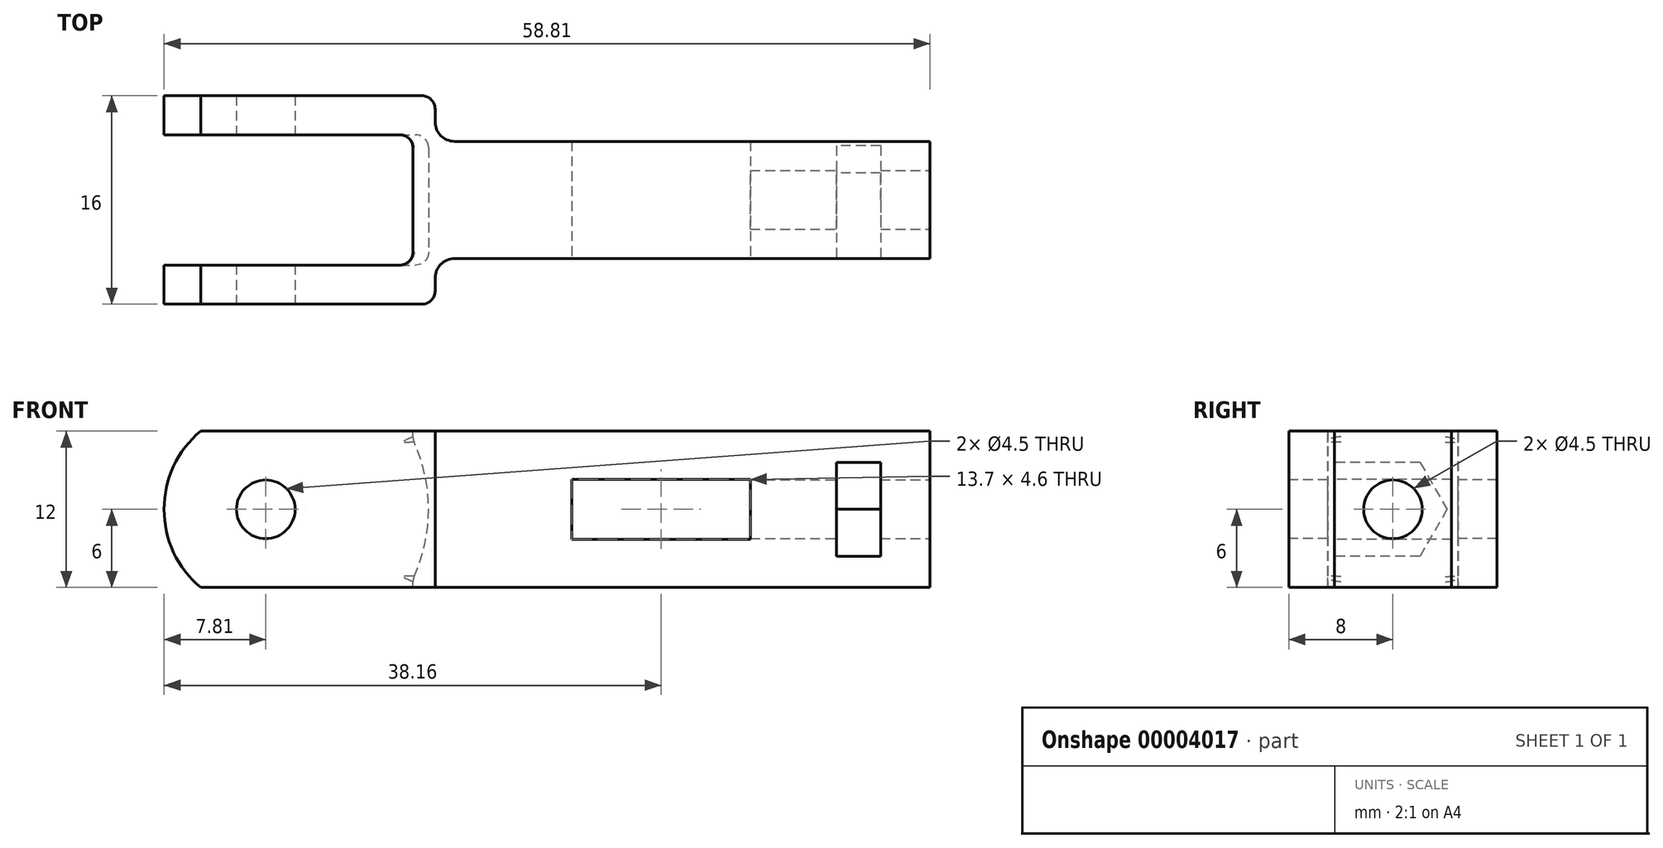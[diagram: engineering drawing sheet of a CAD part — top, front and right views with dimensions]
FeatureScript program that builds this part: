
annotation { "Feature Type Name" : "Feature", "Feature Type Description" : "" }
export const myFeature = defineFeature(function(context is Context, id is Id, definition is map)
    precondition{}
    {
        {
            var Q0;
            Q0=qCreatedBy(makeId("Top.planeOp"),FACE);
            var sketch = newSketch(context, id + "F0", { "sketchPlane" : qUnion([Q0])});
            skLineSegment(sketch, "E0", {"start": v(-5, 8) * mm, "end": v(-5, -8) * mm});
            skLineSegment(sketch, "E1", {"start": v(-5, 8) * mm, "end": v(13, 8) * mm});
            skLineSegment(sketch, "E2", {"start": v(13, 8) * mm, "end": v(13, 4.5) * mm});
            skLineSegment(sketch, "E3", {"start": v(13, 4.5) * mm, "end": v(51, 4.5) * mm});
            skLineSegment(sketch, "E4", {"start": v(51, 4.5) * mm, "end": v(51, -4.5) * mm});
            skLineSegment(sketch, "E5", {"start": v(51, -4.5) * mm, "end": v(13, -4.5) * mm});
            skLineSegment(sketch, "E6", {"start": v(13, -4.5) * mm, "end": v(13, -8) * mm});
            skLineSegment(sketch, "E7", {"start": v(13, -8) * mm, "end": v(-5, -8) * mm});
            skLineSegment(sketch, "E8", {"start": v(0, 0) * mm, "end": v(51, 0) * mm, "construction": true});
            skSolve(sketch);
        }
        {
            var Q0;
            Q0=makeQuery(id+"F0.imprint","IMPRINT",FACE,{"disambiguationData":[TD([[makeQuery(id+"F0.imprint","IMPRINT",EDGE,{"derivedFrom":sQuery(id+"F0.wireOp",EDGE,"E0")}),1.0]])]});
            extrude(context, id + "F1", {"entities" : qUnion([Q0]), "depth" : 12 * mm, "symmetric" : true});
        }
        {
            var Q0;
            Q0=makeQuery(id+"F1.opExtrude","SWEPT_FACE",FACE,{"disambiguationData":[OSD([sQuery(id+"F0.wireOp",EDGE,"E7")])]});
            var sketch = newSketch(context, id + "F2", { "sketchPlane" : qUnion([Q0])});
            skCircle(sketch, "E9", {"center": v(0, 0) * mm, "radius": 2.25 * mm});
            skSolve(sketch);
        }
        {
            var Q0;
            Q0=makeQuery(id+"F2.imprint","IMPRINT",FACE,{"disambiguationData":[TD([[makeQuery(id+"F2.imprint","IMPRINT",EDGE,{"derivedFrom":sQuery(id+"F2.wireOp",EDGE,"E9")}),1.0]])]});
            extrude(context, id + "F3", {"entities" : qUnion([Q0]), "operationType" : NewBodyOperationType.REMOVE, "endBound" : BoundingType.THROUGH_ALL, "oppositeDirection" : true, "depth" : 25 * mm});
        }
        {
            var Q0;
            Q0=makeQuery(id+"F1.opExtrude","SWEPT_FACE",FACE,{"disambiguationData":[OSD([sQuery(id+"F0.wireOp",EDGE,"E7")])]});
            var sketch = newSketch(context, id + "F4", { "sketchPlane" : qUnion([Q0])});
            skArc(sketch, "E10", {"start": v(-5, 6) * mm, "mid": v(-7.81, 0) * mm, "end": v(-5, -6) * mm});
            skLineSegment(sketch, "E11", {"start": v(-5, -6) * mm, "end": v(-5, 6) * mm});
            skSolve(sketch);
        }
        {
            var Q0;
            Q0=makeQuery(id+"F4.imprint","IMPRINT",FACE,{"disambiguationData":[TD([[makeQuery(id+"F4.imprint","IMPRINT",EDGE,{"derivedFrom":sQuery(id+"F4.wireOp",EDGE,"E10")}),1.0]])]});
            var Q1;
            Q1=makeQuery(id+"F1.opExtrude","SWEPT_FACE",FACE,{"disambiguationData":[OSD([sQuery(id+"F0.wireOp",EDGE,"E1")])]});
            extrude(context, id + "F5", {"entities" : qUnion([Q0]), "operationType" : NewBodyOperationType.ADD, "endBound" : BoundingType.UP_TO_SURFACE, "oppositeDirection" : true, "endBoundEntityFace" : qUnion([Q1]), "depth" : 25 * mm});
        }
        {
            var Q0;
            Q0=makeQuery(id+"F1.opExtrude","SWEPT_EDGE",EDGE,{"disambiguationData":[OSD([sQuery(id+"F0.wireOp",EDGE,"E2"),sQuery(id+"F0.wireOp",EDGE,"E3")])]});
            var Q1;
            Q1=makeQuery(id+"F1.opExtrude","SWEPT_EDGE",EDGE,{"disambiguationData":[OSD([sQuery(id+"F0.wireOp",EDGE,"E5"),sQuery(id+"F0.wireOp",EDGE,"E6")])]});
            fillet(context, id + "F6", {"entities" : qUnion([Q0, Q1]), "radius" : 1.5 * mm, "tangentPropagation" : true, "allowEdgeOverflow" : false});
        }
        {
            var Q0;
            Q0=qCreatedBy(makeId("Front.planeOp"),FACE);
            var sketch = newSketch(context, id + "F7", { "sketchPlane" : qUnion([Q0])});
            skArc(sketch, "E12", {"start": v(11.3, -5.34) * mm, "mid": v(12.5, 0) * mm, "end": v(11.3, 5.34) * mm});
            skLineSegment(sketch, "E13", {"start": v(11.3, 5.34) * mm, "end": v(11.3, 6) * mm});
            skLineSegment(sketch, "E14", {"start": v(-5, -6) * mm, "end": v(11.3, -6) * mm});
            skLineSegment(sketch, "E15", {"start": v(11.3, -6) * mm, "end": v(11.3, -5.34) * mm});
            skLineSegment(sketch, "E16", {"start": v(-5, 6) * mm, "end": v(11.3, 6) * mm});
            skArc(sketch, "E17.0", {"start": v(-5, 6) * mm, "mid": v(-7.81, 0) * mm, "end": v(-5, -6) * mm});
            skSolve(sketch);
        }
        {
            var Q0;
            Q0=makeQuery(id+"F7.imprint","IMPRINT",FACE,{"disambiguationData":[TD([[makeQuery(id+"F7.imprint","IMPRINT",EDGE,{"derivedFrom":sQuery(id+"F7.wireOp",EDGE,"E12")}),1.0]])]});
            extrude(context, id + "F8", {"entities" : qUnion([Q0]), "operationType" : NewBodyOperationType.REMOVE, "oppositeDirection" : true, "depth" : 10 * mm, "symmetric" : true});
        }
        {
            var Q0;
            Q0=makeQuery(id+"F1.opExtrude","SWEPT_FACE",FACE,{"disambiguationData":[OSD([sQuery(id+"F0.wireOp",EDGE,"E5")])]});
            var sketch = newSketch(context, id + "F9", { "sketchPlane" : qUnion([Q0])});
            skLineSegment(sketch, "E18", {"start": v(51, 0) * mm, "end": v(30.35, 0) * mm, "construction": true});
            skLineSegment(sketch, "E19.rect.bottom", {"start": v(37.2, 2.3) * mm, "end": v(23.5, 2.3) * mm});
            skLineSegment(sketch, "E19.rect.top", {"start": v(37.2, -2.3) * mm, "end": v(23.5, -2.3) * mm});
            skLineSegment(sketch, "E19.rect.left", {"start": v(37.2, 2.3) * mm, "end": v(37.2, -2.3) * mm});
            skLineSegment(sketch, "E19.rect.right", {"start": v(23.5, 2.3) * mm, "end": v(23.5, -2.3) * mm});
            skPoint(sketch, "E19.rect.middle", {"position": v(30.35, 0) * mm});
            skSolve(sketch);
        }
        {
            var Q0;
            Q0=makeQuery(id+"F9.imprint","IMPRINT",FACE,{"disambiguationData":[TD([[makeQuery(id+"F9.imprint","IMPRINT",EDGE,{"derivedFrom":sQuery(id+"F9.wireOp",EDGE,"E19.rect.bottom")}),1.0]])]});
            extrude(context, id + "F10", {"entities" : qUnion([Q0]), "operationType" : NewBodyOperationType.REMOVE, "endBound" : BoundingType.THROUGH_ALL, "oppositeDirection" : true, "depth" : 25 * mm});
        }
        {
            var Q0;
            Q0=makeQuery(id+"F1.opExtrude","SWEPT_FACE",FACE,{"disambiguationData":[OSD([sQuery(id+"F0.wireOp",EDGE,"E5")])]});
            var sketch = newSketch(context, id + "F11", { "sketchPlane" : qUnion([Q0])});
            skLineSegment(sketch, "E20", {"start": v(51, 0) * mm, "end": v(45.5, 0) * mm, "construction": true});
            skLineSegment(sketch, "E21.rect.bottom", {"start": v(47.2, 3.6) * mm, "end": v(43.8, 3.6) * mm});
            skLineSegment(sketch, "E21.rect.top", {"start": v(47.2, -3.6) * mm, "end": v(43.8, -3.6) * mm});
            skLineSegment(sketch, "E21.rect.left", {"start": v(47.2, 3.6) * mm, "end": v(47.2, -3.6) * mm});
            skLineSegment(sketch, "E21.rect.right", {"start": v(43.8, 3.6) * mm, "end": v(43.8, -3.6) * mm});
            skPoint(sketch, "E21.rect.middle", {"position": v(45.5, 0) * mm});
            skSolve(sketch);
        }
        {
            var Q0;
            Q0=makeQuery(id+"F11.imprint","IMPRINT",FACE,{"disambiguationData":[TD([[makeQuery(id+"F11.imprint","IMPRINT",EDGE,{"derivedFrom":sQuery(id+"F11.wireOp",EDGE,"E21.rect.bottom")}),1.0]])]});
            extrude(context, id + "F12", {"entities" : qUnion([Q0]), "operationType" : NewBodyOperationType.REMOVE, "endBound" : BoundingType.THROUGH_ALL, "oppositeDirection" : true, "depth" : 25 * mm});
        }
        {
            var Q0;
            Q0=makeQuery(id+"F1.opExtrude","SWEPT_FACE",FACE,{"disambiguationData":[OSD([sQuery(id+"F0.wireOp",EDGE,"E4")])]});
            var sketch = newSketch(context, id + "F13", { "sketchPlane" : qUnion([Q0])});
            skCircle(sketch, "E22", {"center": v(0, 0) * mm, "radius": 2.25 * mm});
            skSolve(sketch);
        }
        {
            var Q0;
            Q0=makeQuery(id+"F13.imprint","IMPRINT",FACE,{"disambiguationData":[TD([[makeQuery(id+"F13.imprint","IMPRINT",EDGE,{"derivedFrom":sQuery(id+"F13.wireOp",EDGE,"E22")}),1.0]])]});
            var Q1;
            Q1=makeQuery(id+"F10.boolean.opBoolean","COPY",FACE,{"derivedFrom":makeQuery(id+"F10.opExtrude","SWEPT_FACE",FACE,{"disambiguationData":[OSD([sQuery(id+"F9.wireOp",EDGE,"E19.rect.left")])]})});
            extrude(context, id + "F14", {"entities" : qUnion([Q0]), "operationType" : NewBodyOperationType.REMOVE, "endBound" : BoundingType.UP_TO_SURFACE, "oppositeDirection" : true, "endBoundEntityFace" : qUnion([Q1]), "depth" : 25 * mm});
        }
        {
            var Q0;
            Q0=makeQuery(id+"F12.boolean.opBoolean","COPY",FACE,{"derivedFrom":makeQuery(id+"F12.opExtrude","SWEPT_FACE",FACE,{"disambiguationData":[OSD([sQuery(id+"F11.wireOp",EDGE,"E21.rect.right")])]})});
            var sketch = newSketch(context, id + "F15", { "sketchPlane" : qUnion([Q0])});
            skCircle(sketch, "E23.cCircle", {"center": v(0, 0) * mm, "radius": 3.6 * mm, "construction": true});
            skLineSegment(sketch, "E23.0", {"start": v(-2.08, 3.6) * mm, "end": v(2.08, 3.6) * mm, "construction": true});
            skLineSegment(sketch, "E23.1", {"start": v(2.08, 3.6) * mm, "end": v(4.16, 0) * mm});
            skLineSegment(sketch, "E23.2", {"start": v(4.16, 0) * mm, "end": v(2.08, -3.6) * mm});
            skLineSegment(sketch, "E23.3", {"start": v(2.08, -3.6) * mm, "end": v(-2.08, -3.6) * mm, "construction": true});
            skLineSegment(sketch, "E23.4", {"start": v(-2.08, -3.6) * mm, "end": v(-4.16, 0) * mm, "construction": true});
            skLineSegment(sketch, "E23.5", {"start": v(-4.16, 0) * mm, "end": v(-2.08, 3.6) * mm, "construction": true});
            skPoint(sketch, "E23.0.midPoint", {"position": v(0, 3.6) * mm});
            skSolve(sketch);
        }
        {
            var Q0;
            Q0 = qSketchRegion(id + "F15", true);
            var Q1;
            {var subQ5=sQuery(id+"F15.wireOp",EDGE,"E23.1");Q1=makeQuery(id+"F15.imprint","IMPRINT",FACE,{"disambiguationData":[TD([[makeQuery(id+"F15.imprint","IMPRINT",EDGE,{"derivedFrom":subQ5}),1.0]])]});}
            var Q2;
            {var subQ5=sQuery(id+"F15.wireOp",EDGE,"E23.1");Q2=makeQuery(id+"F15.imprint","IMPRINT",FACE,{"disambiguationData":[TD([[makeQuery(id+"F15.imprint","IMPRINT",EDGE,{"derivedFrom":subQ5}),1.0]])]});}
            var Q3;
            Q3=makeQuery(id+"F12.boolean.opBoolean","COPY",FACE,{"derivedFrom":makeQuery(id+"F12.opExtrude","SWEPT_FACE",FACE,{"disambiguationData":[OSD([sQuery(id+"F11.wireOp",EDGE,"E21.rect.left")])]})});
            extrude(context, id + "F16", {"entities" : qUnion([Q0, Q1, Q2]), "operationType" : NewBodyOperationType.ADD, "endBound" : BoundingType.UP_TO_SURFACE, "endBoundEntityFace" : qUnion([Q3]), "depth" : 25 * mm});
        }
        {
            var Q0;
            Q0=makeQuery(id+"F8.boolean.opBoolean","COPY",EDGE,{"derivedFrom":makeQuery(id+"F8.opExtrude","CAP_EDGE",EDGE,{"disambiguationData":[OSD([sQuery(id+"F7.wireOp",EDGE,"E12")])],"isStart":false})});
            var Q1;
            Q1=makeQuery(id+"F8.boolean.opBoolean","COPY",EDGE,{"derivedFrom":makeQuery(id+"F8.opExtrude","CAP_EDGE",EDGE,{"disambiguationData":[OSD([sQuery(id+"F7.wireOp",EDGE,"E13")])],"isStart":false})});
            var Q2;
            Q2=makeQuery(id+"F8.boolean.opBoolean","COPY",EDGE,{"derivedFrom":makeQuery(id+"F8.opExtrude","CAP_EDGE",EDGE,{"disambiguationData":[OSD([sQuery(id+"F7.wireOp",EDGE,"E15")])],"isStart":false})});
            var Q3;
            Q3=makeQuery(id+"F8.boolean.opBoolean","COPY",EDGE,{"derivedFrom":makeQuery(id+"F8.opExtrude","CAP_EDGE",EDGE,{"disambiguationData":[OSD([sQuery(id+"F7.wireOp",EDGE,"E15")])],"isStart":true})});
            var Q4;
            Q4=makeQuery(id+"F8.boolean.opBoolean","COPY",EDGE,{"derivedFrom":makeQuery(id+"F8.opExtrude","CAP_EDGE",EDGE,{"disambiguationData":[OSD([sQuery(id+"F7.wireOp",EDGE,"E12")])],"isStart":true})});
            var Q5;
            Q5=makeQuery(id+"F8.boolean.opBoolean","COPY",EDGE,{"derivedFrom":makeQuery(id+"F8.opExtrude","CAP_EDGE",EDGE,{"disambiguationData":[OSD([sQuery(id+"F7.wireOp",EDGE,"E13")])],"isStart":true})});
            fillet(context, id + "F17", {"entities" : qUnion([Q0, Q1, Q2, Q3, Q4, Q5]), "radius" : 1 * mm, "tangentPropagation" : true, "allowEdgeOverflow" : false});
        }
        {
            var Q0;
            Q0=makeQuery(id+"F17.opFillet","BLEND_EDGE",EDGE,{"blendedFrom":[makeQuery(id+"F8.boolean.opBoolean","COPY",EDGE,{"derivedFrom":makeQuery(id+"F8.opExtrude","CAP_EDGE",EDGE,{"disambiguationData":[OSD([sQuery(id+"F7.wireOp",EDGE,"E12")])],"isStart":false})}),makeQuery(id+"F8.boolean.opBoolean","COPY",EDGE,{"derivedFrom":makeQuery(id+"F8.opExtrude","CAP_EDGE",EDGE,{"disambiguationData":[OSD([sQuery(id+"F7.wireOp",EDGE,"E15")])],"isStart":false})})],"blendedInto":[]});
            var Q1;
            Q1=makeQuery(id+"F8.boolean.opBoolean","COPY",EDGE,{"derivedFrom":makeQuery(id+"F8.opExtrude","SWEPT_EDGE",EDGE,{"disambiguationData":[OSD([sQuery(id+"F7.wireOp",EDGE,"E12"),sQuery(id+"F7.wireOp",EDGE,"E15")])]})});
            var Q2;
            Q2=makeQuery(id+"F17.opFillet","BLEND_EDGE",EDGE,{"blendedFrom":[makeQuery(id+"F8.boolean.opBoolean","COPY",EDGE,{"derivedFrom":makeQuery(id+"F8.opExtrude","CAP_EDGE",EDGE,{"disambiguationData":[OSD([sQuery(id+"F7.wireOp",EDGE,"E12")])],"isStart":true})}),makeQuery(id+"F8.boolean.opBoolean","COPY",EDGE,{"derivedFrom":makeQuery(id+"F8.opExtrude","CAP_EDGE",EDGE,{"disambiguationData":[OSD([sQuery(id+"F7.wireOp",EDGE,"E15")])],"isStart":true})})],"blendedInto":[]});
            var Q3;
            Q3=makeQuery(id+"F17.opFillet","BLEND_EDGE",EDGE,{"blendedFrom":[makeQuery(id+"F8.boolean.opBoolean","COPY",EDGE,{"derivedFrom":makeQuery(id+"F8.opExtrude","CAP_EDGE",EDGE,{"disambiguationData":[OSD([sQuery(id+"F7.wireOp",EDGE,"E12")])],"isStart":true})}),makeQuery(id+"F8.boolean.opBoolean","COPY",EDGE,{"derivedFrom":makeQuery(id+"F8.opExtrude","CAP_EDGE",EDGE,{"disambiguationData":[OSD([sQuery(id+"F7.wireOp",EDGE,"E13")])],"isStart":true})})],"blendedInto":[]});
            var Q4;
            Q4=makeQuery(id+"F8.boolean.opBoolean","COPY",EDGE,{"derivedFrom":makeQuery(id+"F8.opExtrude","SWEPT_EDGE",EDGE,{"disambiguationData":[OSD([sQuery(id+"F7.wireOp",EDGE,"E12"),sQuery(id+"F7.wireOp",EDGE,"E13")])]})});
            var Q5;
            Q5=makeQuery(id+"F17.opFillet","BLEND_EDGE",EDGE,{"blendedFrom":[makeQuery(id+"F8.boolean.opBoolean","COPY",EDGE,{"derivedFrom":makeQuery(id+"F8.opExtrude","CAP_EDGE",EDGE,{"disambiguationData":[OSD([sQuery(id+"F7.wireOp",EDGE,"E12")])],"isStart":false})}),makeQuery(id+"F8.boolean.opBoolean","COPY",EDGE,{"derivedFrom":makeQuery(id+"F8.opExtrude","CAP_EDGE",EDGE,{"disambiguationData":[OSD([sQuery(id+"F7.wireOp",EDGE,"E13")])],"isStart":false})})],"blendedInto":[]});
            fillet(context, id + "F18", {"entities" : qUnion([Q0, Q1, Q2, Q3, Q4, Q5]), "radius" : 1 * mm, "tangentPropagation" : true, "allowEdgeOverflow" : false});
        }
        {
            var Q0;
            Q0=makeQuery(id+"F1.opExtrude","SWEPT_EDGE",EDGE,{"disambiguationData":[OSD([sQuery(id+"F0.wireOp",EDGE,"E1"),sQuery(id+"F0.wireOp",EDGE,"E2")])]});
            var Q1;
            Q1=makeQuery(id+"F1.opExtrude","SWEPT_EDGE",EDGE,{"disambiguationData":[OSD([sQuery(id+"F0.wireOp",EDGE,"E6"),sQuery(id+"F0.wireOp",EDGE,"E7")])]});
            fillet(context, id + "F19", {"entities" : qUnion([Q0, Q1]), "radius" : 1 * mm, "tangentPropagation" : true, "allowEdgeOverflow" : false});
        }
    });
